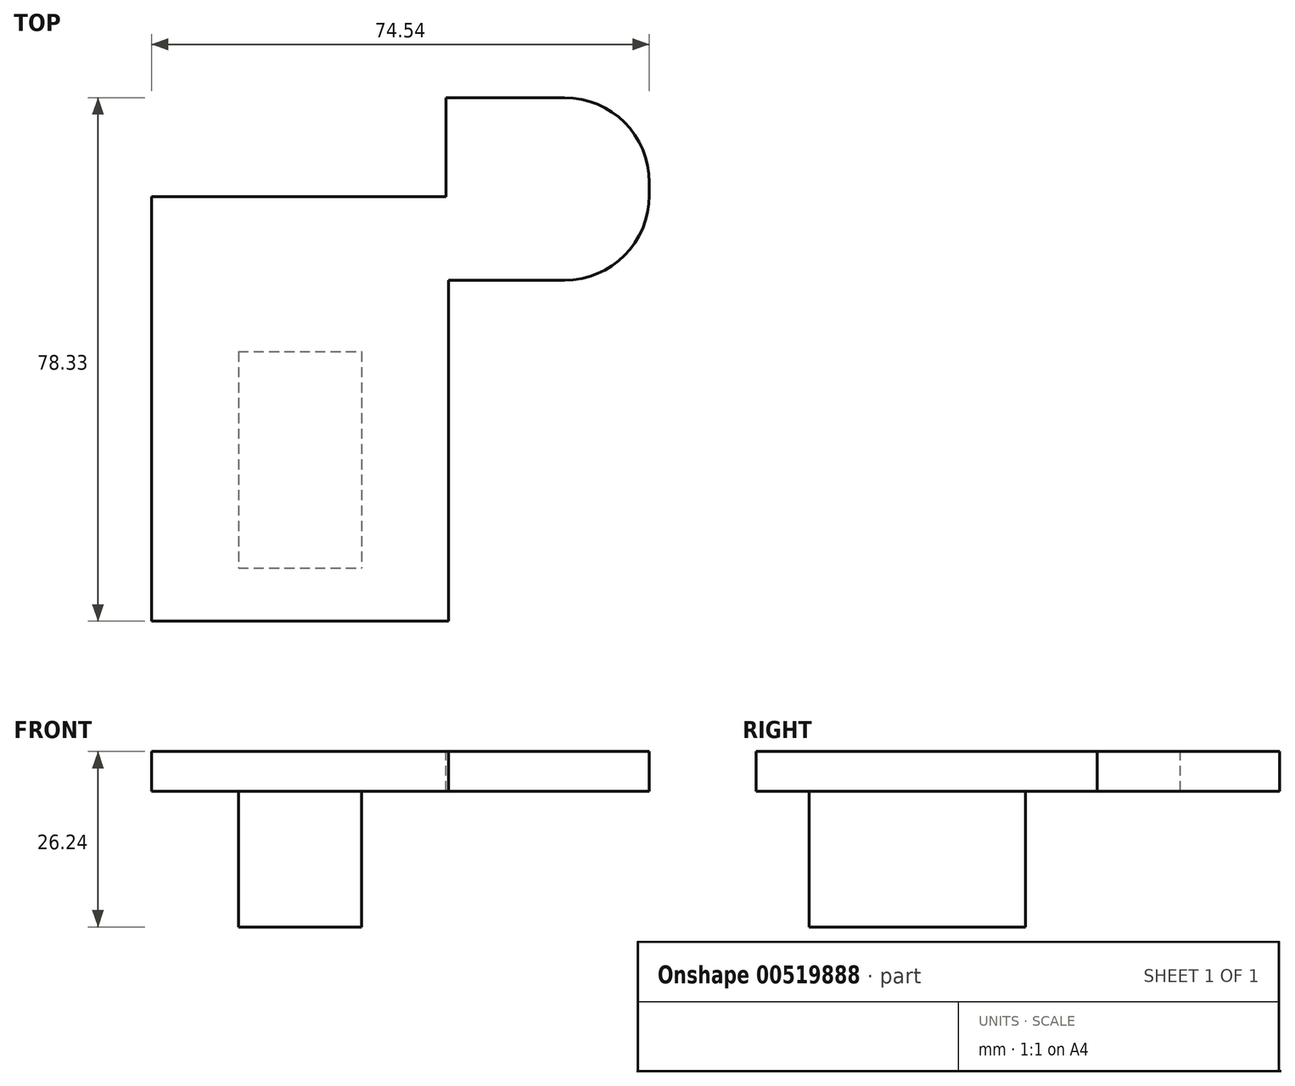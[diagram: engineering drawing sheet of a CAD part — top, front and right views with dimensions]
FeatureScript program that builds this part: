
annotation { "Feature Type Name" : "Feature", "Feature Type Description" : "" }
export const myFeature = defineFeature(function(context is Context, id is Id, definition is map)
    precondition{}
    {
        {
            var Q0;
            Q0=qCreatedBy(makeId("Top.planeOp"),FACE);
            var sketch = newSketch(context, id + "F0", { "sketchPlane" : qUnion([Q0])});
            skLineSegment(sketch, "E0.bottom", {"start": v(22.23, -62.23) * mm, "end": v(-22.22, -62.23) * mm});
            skLineSegment(sketch, "E0.top", {"start": v(22.23, 1.27) * mm, "end": v(-22.23, 1.27) * mm});
            skLineSegment(sketch, "E0.left", {"start": v(22.23, -62.23) * mm, "end": v(22.23, 1.27) * mm});
            skLineSegment(sketch, "E0.right", {"start": v(-22.22, -62.23) * mm, "end": v(-22.22, 1.27) * mm});
            skPoint(sketch, "E0.middle", {"position": v(0, -30.48) * mm});
            skPoint(sketch, "E1", {"position": v(-22.22, -62.23) * mm});
            skPoint(sketch, "E2", {"position": v(22.23, -62.23) * mm});
            skSolve(sketch);
        }
        {
            var Q0;
            Q0=qCreatedBy(makeId("Top.planeOp"),FACE);
            var sketch = newSketch(context, id + "F1", { "sketchPlane" : qUnion([Q0])});
            skLineSegment(sketch, "E3.bottom", {"start": v(21.88, 16.1) * mm, "end": v(39.61, 16.1) * mm});
            skLineSegment(sketch, "E3.top", {"start": v(21.88, -11.2) * mm, "end": v(39.61, -11.2) * mm});
            skLineSegment(sketch, "E3.left", {"start": v(21.88, 16.1) * mm, "end": v(21.88, -11.2) * mm});
            skLineSegment(sketch, "E3.right", {"start": v(52.31, 3.4) * mm, "end": v(52.31, 1.5) * mm});
            skPoint(sketch, "E4.visualSharp", {"position": v(52.31, -11.2) * mm});
            skArc(sketch, "E4.filletArc", {"start": v(39.61, -11.2) * mm, "mid": v(48.6, -7.49) * mm, "end": v(52.31, 1.5) * mm});
            skPoint(sketch, "E5.visualSharp", {"position": v(52.31, 16.1) * mm});
            skArc(sketch, "E5.filletArc", {"start": v(52.31, 3.4) * mm, "mid": v(48.6, 12.38) * mm, "end": v(39.61, 16.1) * mm});
            skSolve(sketch);
        }
        {
            var Q0;
            Q0 = qSketchRegion(id + "F1", true);
            extrude(context, id + "F2", {"entities" : qUnion([Q0]), "depth" : 5.92 * mm, "offsetDistance" : 25.4 * mm});
        }
        {
            var Q0;
            Q0=makeQuery(id+"F0.imprint","IMPRINT",FACE,{"disambiguationData":[TD([[makeQuery(id+"F0.imprint","IMPRINT",EDGE,{"derivedFrom":sQuery(id+"F0.wireOp",EDGE,"E0.bottom")}),-1.0]])]});
            var Q1;
            Q1=makeQuery(id+"F2.opExtrude","CAP_FACE",FACE,{"disambiguationData":[OSD([sQuery(id+"F1.wireOp",EDGE,"E3.bottom"),sQuery(id+"F1.wireOp",EDGE,"E3.top"),sQuery(id+"F1.wireOp",EDGE,"E3.left"),sQuery(id+"F1.wireOp",EDGE,"E3.right"),sQuery(id+"F1.wireOp",EDGE,"E4.filletArc"),sQuery(id+"F1.wireOp",EDGE,"E5.filletArc")])],"isStart":true});
            extrude(context, id + "F3", {"entities" : qUnion([Q0, Q1]), "operationType" : NewBodyOperationType.ADD, "depth" : 5.92 * mm, "offsetDistance" : 25.4 * mm});
        }
        {
            var Q0;
            Q0=qCreatedBy(makeId("Top.planeOp"),FACE);
            var sketch = newSketch(context, id + "F4", { "sketchPlane" : qUnion([Q0])});
            skLineSegment(sketch, "E6.bottom", {"start": v(-9.2, -21.92) * mm, "end": v(9.2, -21.92) * mm});
            skLineSegment(sketch, "E6.top", {"start": v(-9.2, -54.3) * mm, "end": v(9.2, -54.3) * mm});
            skLineSegment(sketch, "E6.left", {"start": v(-9.2, -21.92) * mm, "end": v(-9.2, -54.3) * mm});
            skLineSegment(sketch, "E6.right", {"start": v(9.2, -21.92) * mm, "end": v(9.2, -54.3) * mm});
            skPoint(sketch, "E6.middle", {"position": v(0, -38.11) * mm});
            skSolve(sketch);
        }
        {
            var Q0;
            Q0=makeQuery(id+"F4.imprint","IMPRINT",FACE,{"disambiguationData":[TD([[makeQuery(id+"F4.imprint","IMPRINT",EDGE,{"derivedFrom":sQuery(id+"F4.wireOp",EDGE,"E6.bottom")}),-1.0]])]});
            extrude(context, id + "F5", {"entities" : qUnion([Q0]), "operationType" : NewBodyOperationType.ADD, "oppositeDirection" : true, "depth" : 20.32 * mm, "offsetDistance" : 25.4 * mm});
        }
    });
